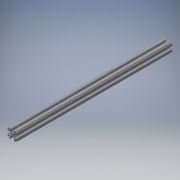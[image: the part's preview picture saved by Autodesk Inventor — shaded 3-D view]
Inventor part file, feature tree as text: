
AUTODESK INVENTOR PART (.ipt)
format: ipt  version: 2017 (Build 210142000, 142)  size: 297,472 bytes
history: native  units: in
note: dims shown in document units (in); Inventor stores cm internally (conversion verified against a paired STEP export)
features: extrude x1, sketch x1, fillet x1
ambient origin geometry x8: Origin, YZ Plane, XZ Plane, XY Plane, X Axis, Y Axis, Z Axis, Center Point
bodies: Solid1 (feature_tree)
feature tree (3):
  extrude  "Extrusion1"  [1 undecoded]
  sketch  "Sketch1"  dims[d0=2.7165in d1=0.0in]
  fillet  "Fillet10"  [1 undecoded]
note: 2 required parameter values undecoded (feature->parameter linkage not recoverable at this tier; creation-order binding heuristic only, values carry confidence <= 0.55)
